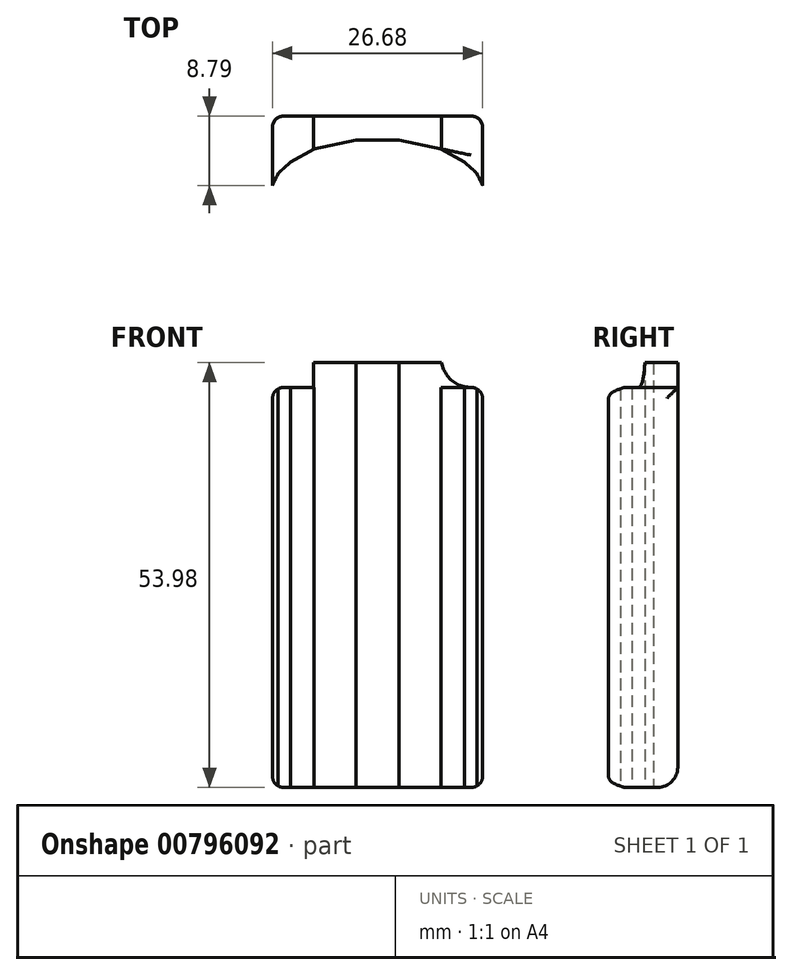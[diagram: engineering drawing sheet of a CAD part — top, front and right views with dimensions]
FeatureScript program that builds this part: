
annotation { "Feature Type Name" : "Feature", "Feature Type Description" : "" }
export const myFeature = defineFeature(function(context is Context, id is Id, definition is map)
    precondition{}
    {
        {
            var Q0;
            Q0=qCreatedBy(makeId("Top.planeOp"),FACE);
            var sketch = newSketch(context, id + "F0", { "sketchPlane" : qUnion([Q0])});
            skLineSegment(sketch, "E0", {"start": v(-9.85, 6.38) * mm, "end": v(16.83, 6.38) * mm});
            skLineSegment(sketch, "E1", {"start": v(-9.12, -0.86) * mm, "end": v(-9.85, -2.41) * mm});
            skLineSegment(sketch, "E2", {"start": v(-9.12, -0.86) * mm, "end": v(-7.55, 0.56) * mm});
            skLineSegment(sketch, "E3", {"start": v(-4.6, 2.2) * mm, "end": v(-7.55, 0.56) * mm});
            skLineSegment(sketch, "E4", {"start": v(-4.6, 2.2) * mm, "end": v(0.76, 3.31) * mm});
            skLineSegment(sketch, "E5.MirrorCS", {"start": v(11.58, 2.2) * mm, "end": v(6.21, 3.31) * mm});
            skLineSegment(sketch, "E6.MirrorCS", {"start": v(11.58, 2.2) * mm, "end": v(14.53, 0.56) * mm});
            skLineSegment(sketch, "E7.MirrorCS", {"start": v(16.1, -0.86) * mm, "end": v(14.53, 0.56) * mm});
            skLineSegment(sketch, "E8.MirrorCS", {"start": v(16.1, -0.86) * mm, "end": v(16.83, -2.41) * mm});
            skLineSegment(sketch, "E9", {"start": v(0.76, 3.31) * mm, "end": v(6.21, 3.31) * mm});
            skLineSegment(sketch, "E10", {"start": v(16.83, 6.38) * mm, "end": v(16.83, -2.41) * mm});
            skLineSegment(sketch, "E11", {"start": v(-9.85, 6.38) * mm, "end": v(-9.85, -2.41) * mm});
            skSolve(sketch);
        }
        {
            var Q0;
            Q0 = qSketchRegion(id + "F0", true);
            extrude(context, id + "F1", {"entities" : qUnion([Q0]), "depth" : 50.8 * mm, "offsetDistance" : 25.4 * mm});
        }
        {
            var Q0;
            Q0=makeQuery(id+"F1.opExtrude","CAP_FACE",FACE,{"disambiguationData":[OSD([sQuery(id+"F0.wireOp",EDGE,"E0"),sQuery(id+"F0.wireOp",EDGE,"E1"),sQuery(id+"F0.wireOp",EDGE,"E2"),sQuery(id+"F0.wireOp",EDGE,"E3"),sQuery(id+"F0.wireOp",EDGE,"E4"),sQuery(id+"F0.wireOp",EDGE,"E5.MirrorCS"),sQuery(id+"F0.wireOp",EDGE,"E6.MirrorCS"),sQuery(id+"F0.wireOp",EDGE,"E7.MirrorCS"),sQuery(id+"F0.wireOp",EDGE,"E8.MirrorCS"),sQuery(id+"F0.wireOp",EDGE,"E9"),sQuery(id+"F0.wireOp",EDGE,"E10"),sQuery(id+"F0.wireOp",EDGE,"E11")])],"isStart":false});
            var sketch = newSketch(context, id + "F2", { "sketchPlane" : qUnion([Q0])});
            skSolve(sketch);
        }
        {
            var Q0;
            Q0=makeQuery(id+"F2.imprint","IMPRINT",FACE,{"disambiguationData":[TD([[makeQuery(id+"F2.imprint","IMPRINT",EDGE,{"derivedFrom":makeQuery(id+"F1.opExtrude","CAP_EDGE",EDGE,{"disambiguationData":[OSD([sQuery(id+"F0.wireOp",EDGE,"E0")])],"isStart":false})}),-1.0]])]});
            var sketch = newSketch(context, id + "F3", { "sketchPlane" : qUnion([Q0])});
            skLineSegment(sketch, "E12.bottom", {"start": v(-4.64, 6.38) * mm, "end": v(11.62, 6.38) * mm});
            skLineSegment(sketch, "E12.left", {"start": v(-4.64, 6.38) * mm, "end": v(-4.64, 2.2) * mm});
            skLineSegment(sketch, "E12.right", {"start": v(11.62, 6.38) * mm, "end": v(11.62, 2.2) * mm});
            skPoint(sketch, "E12.middle", {"position": v(3.49, 4.3) * mm});
            skLineSegment(sketch, "E13", {"start": v(-4.64, 2.2) * mm, "end": v(0.76, 3.31) * mm});
            skLineSegment(sketch, "E14", {"start": v(0.76, 3.31) * mm, "end": v(6.21, 3.31) * mm});
            skLineSegment(sketch, "E15", {"start": v(6.21, 3.31) * mm, "end": v(11.62, 2.2) * mm});
            skSolve(sketch);
        }
        {
            var Q0;
            Q0 = qSketchRegion(id + "F3", true);
            extrude(context, id + "F4", {"entities" : qUnion([Q0]), "operationType" : NewBodyOperationType.ADD, "depth" : 3.17 * mm, "offsetDistance" : 25.4 * mm});
        }
        {
            var Q0;
            Q0=makeQuery(id+"F4.opExtrude","CAP_EDGE",EDGE,{"disambiguationData":[OSD([sQuery(id+"F3.wireOp",EDGE,"E12.right")])],"isStart":true});
            var Q1;
            Q1=makeQuery(id+"F4.opExtrude","CAP_EDGE",EDGE,{"disambiguationData":[OSD([sQuery(id+"F3.wireOp",EDGE,"E12.left")])],"isStart":true});
            fillet(context, id + "F5", {"entities" : qUnion([Q0, Q1]), "radius" : 3.8 * mm, "tangentPropagation" : true, "allowEdgeOverflow" : false});
        }
        {
            var Q0;
            Q0=makeQuery(id+"F1.opExtrude","CAP_EDGE",EDGE,{"disambiguationData":[OSD([sQuery(id+"F0.wireOp",EDGE,"E11")])],"isStart":false});
            var Q1;
            Q1=makeQuery(id+"F1.opExtrude","CAP_EDGE",EDGE,{"disambiguationData":[OSD([sQuery(id+"F0.wireOp",EDGE,"E10")])],"isStart":false});
            var Q2;
            Q2=makeQuery(id+"F1.opExtrude","CAP_EDGE",EDGE,{"disambiguationData":[OSD([sQuery(id+"F0.wireOp",EDGE,"E10")])],"isStart":true});
            var Q3;
            Q3=makeQuery(id+"F1.opExtrude","CAP_EDGE",EDGE,{"disambiguationData":[OSD([sQuery(id+"F0.wireOp",EDGE,"E11")])],"isStart":true});
            var Q4;
            Q4=makeQuery(id+"F1.opExtrude","SWEPT_EDGE",EDGE,{"disambiguationData":[OSD([sQuery(id+"F0.wireOp",EDGE,"E0"),sQuery(id+"F0.wireOp",EDGE,"E10")])]});
            var Q5;
            Q5=makeQuery(id+"F1.opExtrude","SWEPT_EDGE",EDGE,{"disambiguationData":[OSD([sQuery(id+"F0.wireOp",EDGE,"E0"),sQuery(id+"F0.wireOp",EDGE,"E11")])]});
            fillet(context, id + "F6", {"entities" : qUnion([Q0, Q1, Q2, Q3, Q4, Q5]), "radius" : 1.4 * mm, "tangentPropagation" : true, "allowEdgeOverflow" : false});
        }
        {
            var Q0;
            Q0=makeQuery(id+"F1.opExtrude","CAP_EDGE",EDGE,{"disambiguationData":[OSD([sQuery(id+"F0.wireOp",EDGE,"E0")])],"isStart":true});
            fillet(context, id + "F7", {"entities" : qUnion([Q0]), "radius" : 2.54 * mm, "tangentPropagation" : true, "allowEdgeOverflow" : false});
        }
    });
